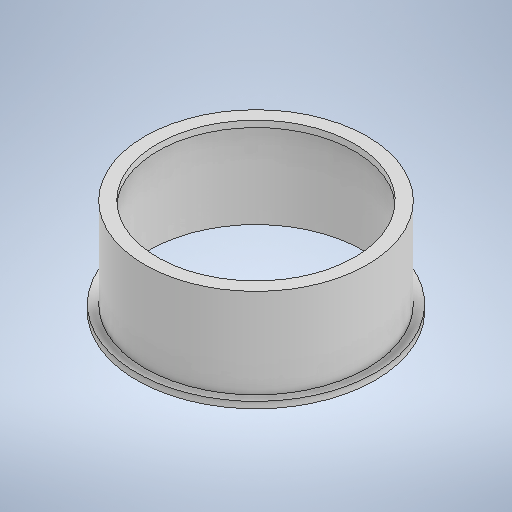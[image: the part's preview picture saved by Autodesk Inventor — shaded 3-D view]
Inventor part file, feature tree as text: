
AUTODESK INVENTOR PART (.ipt)
format: ipt  version: 2025.2 (Build 292293000, 293)  size: 325,120 bytes
history: native  units: in
note: dims shown in document units (in); Inventor stores cm internally (conversion verified against a paired STEP export)
features: other x12, sketch x9, extrude x6, plane x1
ambient origin geometry x8: Origin, YZ Plane, XZ Plane, XY Plane, X Axis, Y Axis, Z Axis, Center Point
bodies: Solid1 (feature_tree)
feature tree (28):
  other  "Table"
  other  "C .Replace - 01"
  other  "C .Replace - 02"
  other  "C .Replace - 03"
  other  "C .Replace - 04"
  other  "C .Replace - 05"
  other  "C .Replace - 06"
  other  "C .Replace - 07"
  other  "C .Replace - 08"
  other  "C .Replace - 09"
  other  "C .Replace - 10"
  other  "C .Replace - Face"
  sketch  "Sketch1"  dims[d5=0.0in d7=0.0in]
  extrude  "Extrusion1"  TaperAngle=0.0deg  [1 undecoded]
  extrude  "Extrusion2"  Depth=10.0394in
  sketch  "Sketch2"  dims[d28=0.1969in d29=3.937in d31=360.0deg]
  extrude  "Extrusion7"  Depth=3.937in TaperAngle=360.0deg
  plane  "Work Plane2"
  extrude  "Extrusion8"  Depth=0.3937in
  extrude  "Extrusion30"  Depth=0.2165in
  sketch  "Sketch25"  dims[d240=2.3622in d242=360.0deg]
  extrude  "Extrusion31"  Depth=0.3937in TaperAngle=0.0deg
  sketch  "Sketch3"  dims[d33=0.3937in d34=0.0in d52=4.5276in]
  sketch  "Sketch Circular Pattern1"  dims[d18=0.0in d27=10.0394in]
  sketch  "Sketch24"  dims[d239=0.2559in]
  sketch  "Sketch Circular Pattern4"  dims[d230=4.0157in d231=0.2165in]
  sketch  "Sketch26"  dims[d244=0.1969in d245=0.0in d113=0.0197in d114=0.0344in d115=0.0197in d116=0.0344in d167=0.0197in d168=0.0344in d169=0.0197in d170=0.0344in d215=0.0197in d216=0.0344in d217=0.0197in d218=0.0344in d219=0.0in d220=0.0in]
  sketch  "Sketch Circular Pattern5"  dims[d232=2.3622in d234=360.0deg d236=0.3937in d237=0.0in]
note: 1 required parameter value undecoded (feature->parameter linkage not recoverable at this tier; creation-order binding heuristic only, values carry confidence <= 0.55)
